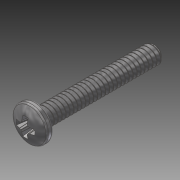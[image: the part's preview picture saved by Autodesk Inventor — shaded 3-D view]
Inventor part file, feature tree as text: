
AUTODESK INVENTOR PART (.ipt)
format: ipt  version: 2014 SP1 (Build 180222100, 222)  size: 916,992 bytes
history: native  units: in
note: dims shown in document units (in); Inventor stores cm internally (conversion verified against a paired STEP export)
features: fillet x1, other x1, imported_body x1
ambient origin geometry x8: Origin, YZ Plane, XZ Plane, XY Plane, X Axis, Y Axis, Z Axis, Center Point
bodies: Body1 (feature_tree)
feature tree (3):
  fillet  "Fillet1"  [1 undecoded]
  other  "91772A1131"
  imported_body  "Base1"
note: 1 required parameter value undecoded (feature->parameter linkage not recoverable at this tier; creation-order binding heuristic only, values carry confidence <= 0.55)
